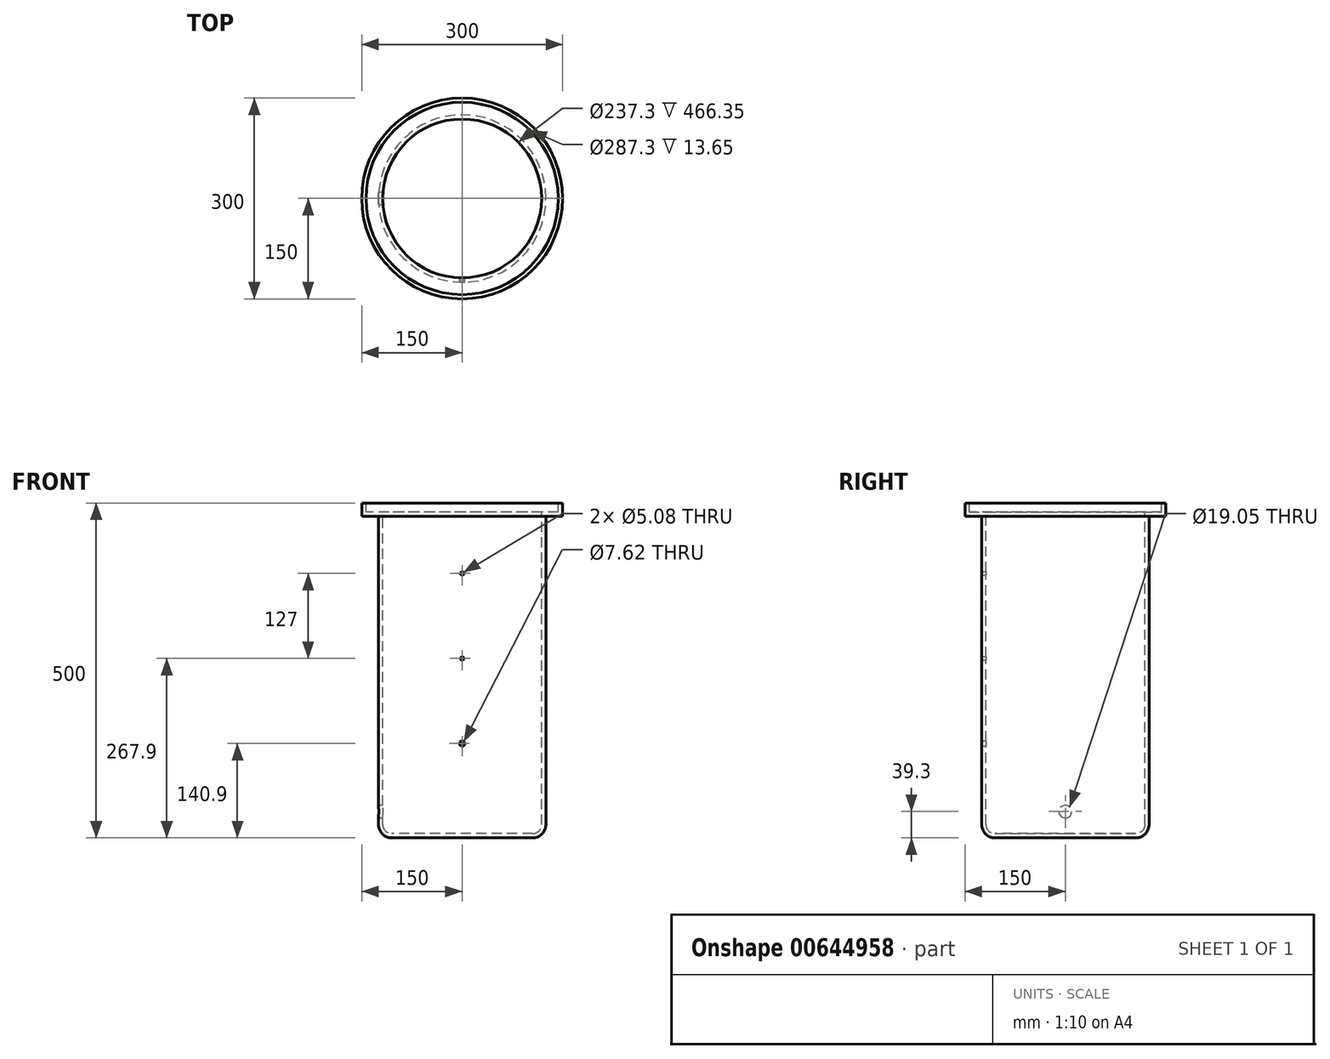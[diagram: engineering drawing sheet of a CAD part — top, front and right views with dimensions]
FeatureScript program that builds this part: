
annotation { "Feature Type Name" : "Feature", "Feature Type Description" : "" }
export const myFeature = defineFeature(function(context is Context, id is Id, definition is map)
    precondition{}
    {
        {
            var Q0;
            Q0=qCreatedBy(makeId("Front.planeOp"),FACE);
            var sketch = newSketch(context, id + "F0", { "sketchPlane" : qUnion([Q0])});
            skLineSegment(sketch, "E0", {"start": v(0, -242.5) * mm, "end": v(105, -242.5) * mm});
            skLineSegment(sketch, "E1", {"start": v(125, -222.5) * mm, "end": v(125, 237.5) * mm});
            skLineSegment(sketch, "E2", {"start": v(125, 237.5) * mm, "end": v(150, 237.5) * mm});
            skLineSegment(sketch, "E3", {"start": v(150, 237.5) * mm, "end": v(150, 257.5) * mm});
            skLineSegment(sketch, "E4", {"start": v(150, 257.5) * mm, "end": v(0, 257.5) * mm});
            skLineSegment(sketch, "E5", {"start": v(0, 257.5) * mm, "end": v(0, -242.5) * mm});
            skPoint(sketch, "E6.visualSharp", {"position": v(125, -242.5) * mm});
            skArc(sketch, "E6.filletArc", {"start": v(105, -242.5) * mm, "mid": v(119.14, -236.64) * mm, "end": v(125, -222.5) * mm});
            skSolve(sketch);
        }
        {
            var Q0;
            Q0=qSketchRegion(id+"F0",true);
            var Q1;
            Q1=sQuery(id+"F0.wireOp",EDGE,"E5");
            revolve(context, id + "F1", {"entities" : qUnion([Q0]), "axis" : qUnion([Q1]), "revolveType" : RevolveType.FULL});
        }
        {
            var Q0;
            Q0=makeQuery(id+"F1.opRevolve","SWEPT_FACE",FACE,{"disambiguationData":[OSD([sQuery(id+"F0.wireOp",EDGE,"E4")])]});
            shell(context, id + "F2", {"entities" : qUnion([Q0]), "thickness" : 6.35 * mm});
        }
        {
            var Q0;
            Q0=qCreatedBy(makeId("Front.planeOp"),FACE);
            var sketch = newSketch(context, id + "F3", { "sketchPlane" : qUnion([Q0])});
            skCircle(sketch, "E7", {"center": v(0, 152.4) * mm, "radius": 2.54 * mm});
            skCircle(sketch, "E8", {"center": v(0, 25.4) * mm, "radius": 2.54 * mm});
            skCircle(sketch, "E9", {"center": v(0, -101.6) * mm, "radius": 3.81 * mm});
            skLineSegment(sketch, "E10", {"start": v(0, 0) * mm, "end": v(0, -127) * mm});
            skLineSegment(sketch, "E11", {"start": v(0, 0) * mm, "end": v(0, 155.55) * mm});
            skSolve(sketch);
        }
        {
            var Q0;
            Q0 = qSketchRegion(id + "F3", true);
            extrude(context, id + "F4", {"entities" : qUnion([Q0]), "operationType" : NewBodyOperationType.REMOVE, "endBound" : BoundingType.THROUGH_ALL, "depth" : 25.4 * mm, "offsetDistance" : 25.4 * mm});
        }
        {
            var Q0;
            Q0=qCreatedBy(makeId("Right.planeOp"),FACE);
            var sketch = newSketch(context, id + "F5", { "sketchPlane" : qUnion([Q0])});
            skLineSegment(sketch, "E12", {"start": v(0, 0) * mm, "end": v(0, -203.2) * mm});
            skCircle(sketch, "E13", {"center": v(0, -203.2) * mm, "radius": 9.53 * mm});
            skSolve(sketch);
        }
        {
            var Q0;
            Q0 = qSketchRegion(id + "F5", true);
            extrude(context, id + "F6", {"entities" : qUnion([Q0]), "operationType" : NewBodyOperationType.REMOVE, "endBound" : BoundingType.THROUGH_ALL, "oppositeDirection" : true, "depth" : 25.4 * mm, "offsetDistance" : 25.4 * mm});
        }
    });
